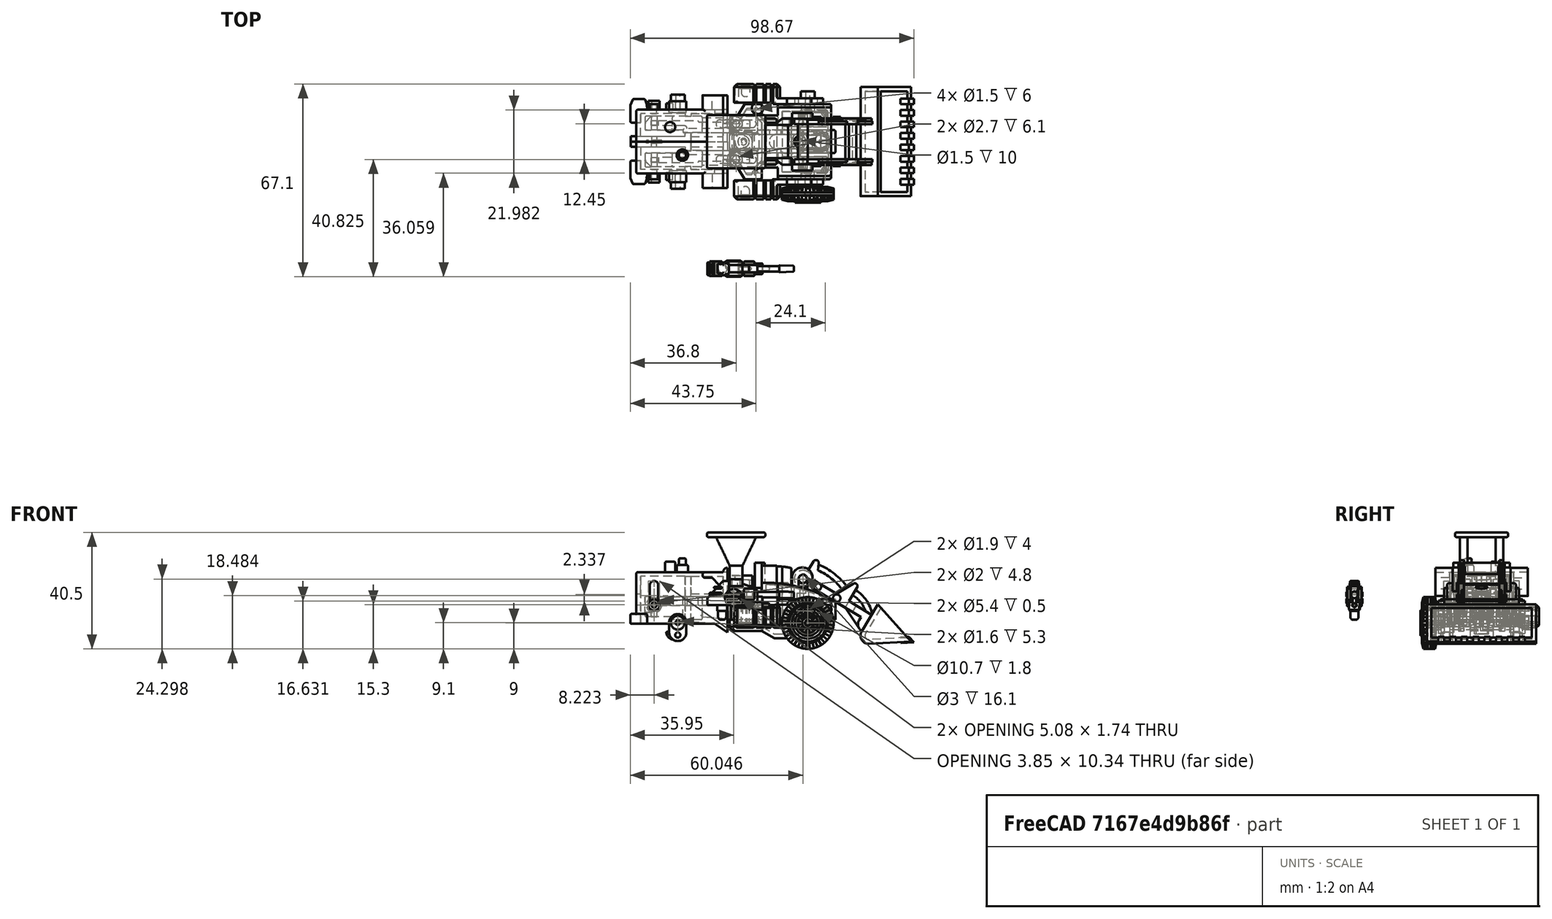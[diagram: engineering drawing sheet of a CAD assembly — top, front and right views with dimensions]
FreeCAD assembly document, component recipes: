
FREECAD ASSEMBLY — COMPONENT RECIPES ("Scrapper")

This assembly document has 14 components, labeled P0..P13 below (a component is one placed body or linked part). 14 of them carry a construction recipe — the FreeCAD feature program that regenerates the part from scratch, quoted from this document or its linked companion documents; the rest are supplied as boundary geometry only. No exploded tour is included for this assembly.
NOTE — document 4 of 4 of this assembly tour. The two overview renders and the header above are repeated from document 1; the component sections below continue where the previous document stopped.
COMPONENT P13 — recipe-attached ("Head", modeled in this document).
Construction recipe (the document's own serialized feature program — sketch geometry with constraints, then the solid features built on it; lengths are millimeters unless a unit is written):

FEATURE [Sketcher::SketchObject] Sketch256
  ArcFitTolerance = 1e-06
  AttachmentSupport = -> [XY_Plane009]
  FullyConstrained = true
  MakeInternals = false
  MapMode = 5
  sketch-geometry (6):
    g0: LineSegment StartX=0 StartY=0 StartZ=0 EndX=17 EndY=0 EndZ=0
    g1: LineSegment StartX=0 StartY=8 StartZ=0 EndX=17 EndY=8 EndZ=0
    g2: ArcOfCircle CenterX=17 CenterY=7.25 CenterZ=0 NormalX=0 NormalY=0 NormalZ=1 AngleXU=0 Radius=0.75 StartAngle=4.71239 EndAngle=7.85398
    g3: ArcOfCircle CenterX=17 CenterY=0.75 CenterZ=0 NormalX=0 NormalY=0 NormalZ=1 AngleXU=0 Radius=0.75 StartAngle=4.71239 EndAngle=7.85398
    g4: LineSegment StartX=0 StartY=8 StartZ=0 EndX=0 EndY=0 EndZ=0
    g5: LineSegment StartX=17 StartY=6.5 StartZ=0 EndX=17 EndY=1.5 EndZ=0
  constraints (19):
    c: Coincident(g0,g-1)
    c: PointOnObject(g0,g-1)
    c: PointOnObject(g1,g-2)
    c: Horizontal(g1)
    c: Coincident(g2,g1)
    c: Coincident(g3,g0)
    c: Coincident(g4,g1)
    c: Coincident(g4,g0)
    c: Coincident(g5,g2)
    c: Coincident(g5,g3)
    c: Vertical(g5)
    c: DistanceY(g4,g4) = 8
    c: DistanceY(g5,g5) = 5
    c: Diameter(g2) = 1.5
    c: Diameter(g3) = 1.5
    c: DistanceX(g3,g0) = 0
    c: DistanceX(g3,g3) = 0
    c: DistanceX(g0,g0) = 17
    c: DistanceX(g1,g1) = 17
FEATURE [PartDesign::Pad] Pad154
  Direction = (0,0,1)
  Length = 1
  Length2 = 10
  Profile = -> Sketch256
  ReferenceAxis = -> Sketch256 [N_Axis]
  Refine = true
  Suppressed = false
  Type = 0
FEATURE [Sketcher::SketchObject] Sketch257
  ArcFitTolerance = 1e-06
  AttachmentSupport = -> [Pad154]
  ExternalGeometry = -> [Pad154]
  FullyConstrained = true
  MakeInternals = false
  MapMode = 5
  Placement = pos=(0,0,1) rot=(0,0,1;0rad)
  sketch-geometry (4):
    g0: ArcOfCircle CenterX=3.2 CenterY=4 CenterZ=0 NormalX=0 NormalY=0 NormalZ=1 AngleXU=0 Radius=2.5 StartAngle=1.5708 EndAngle=4.71239
    g1: ArcOfCircle CenterX=11 CenterY=4 CenterZ=0 NormalX=0 NormalY=0 NormalZ=1 AngleXU=0 Radius=2.5 StartAngle=4.71239 EndAngle=7.85398
    g2: LineSegment StartX=3.2 StartY=6.5 StartZ=0 EndX=11 EndY=6.5 EndZ=0
    g3: LineSegment StartX=3.2 StartY=1.5 StartZ=0 EndX=11 EndY=1.5 EndZ=0
  constraints (11):
    c: Tangent(g0,g2) = 1.5708
    c: Tangent(g0,g3) = -1.5708
    c: Tangent(g1,g2) = 1.5708
    c: Tangent(g1,g3) = -1.5708
    c: Equal(g0,g1)
    c: Horizontal(g2)
    c: Diameter(g0) = 5
    c: DistanceX(g1,g-3) = 6
    c: DistanceX(g0,g1) = 7.8
    c: DistanceY(g-1,g-4) = 8
    c: DistanceY(g0,g-4) = 4
FEATURE [PartDesign::Pocket] Pocket106
  BaseFeature = -> Pad154
  Direction = (0,0,-1)
  Length = 5
  Length2 = 5
  Profile = -> Sketch257
  ReferenceAxis = -> Sketch257 [N_Axis]
  Refine = true
  Suppressed = false
  Type = 0
FEATURE [Sketcher::SketchObject] Sketch258
  ArcFitTolerance = 1e-06
  AttachmentSupport = -> [Pocket106]
  ExternalGeometry = -> [Pocket106]
  FullyConstrained = true
  MakeInternals = false
  MapMode = 5
  Placement = pos=(0,0,0) rot=(1,0,0;1.5708rad)
  sketch-geometry (4):
    g0: LineSegment StartX=0 StartY=1 StartZ=0 EndX=0 EndY=5 EndZ=0
    g1: LineSegment StartX=0 StartY=5 StartZ=0 EndX=9.5 EndY=5 EndZ=0
    g2: LineSegment StartX=9.5 StartY=5 StartZ=0 EndX=13.5 EndY=1 EndZ=0
    g3: LineSegment StartX=13.5 StartY=1 StartZ=0 EndX=0 EndY=1 EndZ=0
  constraints (11):
    c: Coincident(g0,g-3)
    c: PointOnObject(g0,g-2)
    c: Coincident(g1,g0)
    c: Horizontal(g1)
    c: Coincident(g2,g1)
    c: PointOnObject(g2,g-3)
    c: Coincident(g3,g2)
    c: Coincident(g3,g0)
    c: DistanceX(g2,g-3) = 3.5
    c: DistanceY(g0,g0) = 4
    c: Angle(g2,g3) = 0.785398
FEATURE [PartDesign::Pad] Pad155
  BaseFeature = -> Pocket106
  Direction = (0,-1,2e-16)
  Length = 8
  Length2 = 10
  Profile = -> Sketch258
  ReferenceAxis = -> Sketch258 [N_Axis]
  Refine = true
  Reversed = true
  Suppressed = false
  Type = 0
FEATURE [Sketcher::SketchObject] Sketch259
  ArcFitTolerance = 1e-06
  AttachmentSupport = -> [Pad155]
  ExternalGeometry = -> [Pad155]
  FullyConstrained = true
  MakeInternals = false
  MapMode = 5
  Placement = pos=(0,2e-16,1) rot=(1,0,0;3.14159rad)
  sketch-geometry (4):
    g0: ArcOfCircle CenterX=3.2 CenterY=-4 CenterZ=0 NormalX=0 NormalY=0 NormalZ=1 AngleXU=0 Radius=2.5 StartAngle=1.5708 EndAngle=4.71239
    g1: ArcOfCircle CenterX=11 CenterY=-4 CenterZ=0 NormalX=0 NormalY=0 NormalZ=1 AngleXU=0 Radius=2.5 StartAngle=4.71239 EndAngle=7.85398
    g2: LineSegment StartX=11 StartY=-1.5 StartZ=0 EndX=3.2 EndY=-1.5 EndZ=0
    g3: LineSegment StartX=11 StartY=-6.5 StartZ=0 EndX=3.2 EndY=-6.5 EndZ=0
  constraints (8):
    c: Tangent(g0,g-4) = -1.5708
    c: Coincident(g0,g-6)
    c: Coincident(g1,g-5)
    c: Tangent(g1,g-7) = -1.5708
    c: Coincident(g2,g0)
    c: Coincident(g3,g1)
    c: Coincident(g3,g-4)
    c: Coincident(g2,g1)
FEATURE [PartDesign::Pocket] Pocket107
  BaseFeature = -> Pad155
  Direction = (0,0,1)
  Length = 5
  Length2 = 5
  Profile = -> Sketch259
  ReferenceAxis = -> Sketch259 [N_Axis]
  Refine = true
  Suppressed = false
  Type = 0
FEATURE [Sketcher::SketchObject] Sketch260
  ArcFitTolerance = 1e-06
  AttachmentSupport = -> [Pocket107]
  ExternalGeometry = -> [Pocket107]
  FullyConstrained = true
  MakeInternals = false
  MapMode = 5
  Placement = pos=(17,0,0) rot=(0.57735,0.57735,0.57735;2.0944rad)
  sketch-geometry (4):
    g0: LineSegment StartX=1.5 StartY=5 StartZ=0 EndX=6.5 EndY=5 EndZ=0
    g1: LineSegment StartX=1.5 StartY=5 StartZ=0 EndX=1.5 EndY=1 EndZ=0
    g2: LineSegment StartX=6.5 StartY=5 StartZ=0 EndX=6.5 EndY=1 EndZ=0
    g3: LineSegment StartX=6.5 StartY=1 StartZ=0 EndX=1.5 EndY=1 EndZ=0
  constraints (8):
    c: Coincident(g0,g-3)
    c: Coincident(g0,g-4)
    c: Coincident(g1,g0)
    c: Coincident(g1,g-5)
    c: Coincident(g2,g0)
    c: Coincident(g2,g-5)
    c: Coincident(g3,g2)
    c: Coincident(g3,g1)
FEATURE [PartDesign::Pocket] Pocket108
  BaseFeature = -> Pocket107
  Direction = (-1,0,0)
  Length = 9
  Length2 = 5
  Profile = -> Sketch260
  ReferenceAxis = -> Sketch260 [N_Axis]
  Refine = true
  Suppressed = false
  Type = 0
FEATURE [Sketcher::SketchObject] Sketch261
  ArcFitTolerance = 1e-06
  AttachmentSupport = -> [Pocket108]
  ExternalGeometry = -> [Pocket108]
  FullyConstrained = true
  MakeInternals = false
  MapMode = 5
  Placement = pos=(0,1.1e-15,5) rot=(0,0,1;0rad)
  sketch-geometry (4):
    g0: LineSegment StartX=0 StartY=8 StartZ=0 EndX=-8 EndY=8 EndZ=0
    g1: LineSegment StartX=-8 StartY=8 StartZ=0 EndX=-8 EndY=0 EndZ=0
    g2: LineSegment StartX=-8 StartY=0 StartZ=0 EndX=0 EndY=0 EndZ=0
    g3: LineSegment StartX=0 StartY=0 StartZ=0 EndX=0 EndY=8 EndZ=0
  constraints (11):
    c: Coincident(g0,g1)
    c: Coincident(g1,g2)
    c: Coincident(g2,g3)
    c: Coincident(g3,g0)
    c: Horizontal(g0)
    c: Horizontal(g2)
    c: Vertical(g1)
    c: Vertical(g3)
    c: Coincident(g0,g-3)
    c: PointOnObject(g1,g-1)
    c: DistanceX(g0,g0) = 8
FEATURE [PartDesign::Pad] Pad156
  BaseFeature = -> Pocket108
  Direction = (0,0,1)
  Length = 1.5
  Length2 = 10
  Profile = -> Sketch261
  ReferenceAxis = -> Sketch261 [N_Axis]
  Refine = true
  Reversed = true
  Suppressed = false
  Type = 0
FEATURE [Sketcher::SketchObject] Sketch262
  ArcFitTolerance = 1e-06
  AttachmentSupport = -> [Pad156]
  ExternalGeometry = -> [Pad156]
  FullyConstrained = true
  MakeInternals = false
  MapMode = 5
  Placement = pos=(-8,0,0) rot=(0.57735,-0.57735,-0.57735;2.0944rad)
  sketch-geometry (4):
    g0: LineSegment StartX=-8 StartY=7 StartZ=0 EndX=-8 EndY=0 EndZ=0
    g1: LineSegment StartX=-8 StartY=0 StartZ=0 EndX=-1.8e-15 EndY=0 EndZ=0
    g2: LineSegment StartX=-1.8e-15 StartY=0 StartZ=0 EndX=-1.8e-15 EndY=7 EndZ=0
    g3: LineSegment StartX=-1.8e-15 StartY=7 StartZ=0 EndX=-8 EndY=7 EndZ=0
  constraints (12):
    c: Coincident(g0,g1)
    c: Coincident(g1,g2)
    c: Coincident(g2,g3)
    c: Coincident(g3,g0)
    c: Vertical(g0)
    c: Vertical(g2)
    c: Horizontal(g1)
    c: Horizontal(g3)
    c: DistanceX(g3,g3) = 8
    c: DistanceY(g0,g0) = 7
    c: PointOnObject(g-4,g0)
    c: DistanceY(g-4,g0) = 2
FEATURE [PartDesign::Pad] Pad157
  BaseFeature = -> Pad156
  Direction = (-1,0,0)
  Length = 1.5
  Length2 = 10
  Profile = -> Sketch262
  ReferenceAxis = -> Sketch262 [N_Axis]
  Refine = true
  Suppressed = false
  Type = 0
FEATURE [PartDesign::Fillet] Fillet009
  Base = -> Pad157 [Edge56,Edge57,Edge5,Edge50,Edge7,Edge51]
  BaseFeature = -> Pad157
  Radius = 0.5
  Refine = true
  SupportTransform = false
  Suppressed = false
  UseAllEdges = false
FEATURE [Sketcher::SketchObject] Sketch263
  ArcFitTolerance = 1e-06
  AttachmentSupport = -> [Fillet009]
  ExternalGeometry = -> [Fillet009]
  FullyConstrained = true
  MakeInternals = false
  MapMode = 5
  Placement = pos=(0,0,5) rot=(0,0,1;0rad)
  sketch-geometry (1):
    g0: Circle CenterX=-4.55 CenterY=4 CenterZ=0 NormalX=0 NormalY=0 NormalZ=1 AngleXU=0 Radius=2.35
  constraints (5):
    c: Diameter(g0) = 4.7
    c: DistanceY(g-5,g-5) = 7
    c: DistanceY(g0,g-5) = 3.5
    c: Radius(g-6) = 2.5
    c: DistanceX(g0,g-6) = 7.75
FEATURE [PartDesign::Pocket] Pocket109
  BaseFeature = -> Fillet009
  Direction = (0,0,-1)
  Length = 0.7
  Length2 = 5
  Profile = -> Sketch263
  ReferenceAxis = -> Sketch263 [N_Axis]
  Refine = true
  Suppressed = false
  Type = 0
FEATURE [Sketcher::SketchObject] Sketch265
  ArcFitTolerance = 1e-06
  AttachmentSupport = -> [Pocket109]
  ExternalGeometry = -> [Pocket109]
  FullyConstrained = true
  MakeInternals = false
  MapMode = 5
  Placement = pos=(0,0,3.5) rot=(1,0,0;3.14159rad)
  sketch-geometry (6):
    g0: LineSegment StartX=0 StartY=-0.5 StartZ=0 EndX=0 EndY=-7.5 EndZ=0
    g1: LineSegment StartX=0 StartY=-7.5 StartZ=0 EndX=-4 EndY=-7.5 EndZ=0
    g2: LineSegment StartX=-4 StartY=-7.5 StartZ=0 EndX=-7.25 EndY=-6 EndZ=0
    g3: LineSegment StartX=-7.25 StartY=-6 StartZ=0 EndX=-7.25 EndY=-2 EndZ=0
    g4: LineSegment StartX=-7.25 StartY=-2 StartZ=0 EndX=-4 EndY=-0.5 EndZ=0
    g5: LineSegment StartX=-4 StartY=-0.5 StartZ=0 EndX=0 EndY=-0.5 EndZ=0
  constraints (19):
    c: PointOnObject(g0,g-3)
    c: PointOnObject(g0,g-3)
    c: Coincident(g1,g0)
    c: Horizontal(g1)
    c: Coincident(g2,g1)
    c: Coincident(g3,g2)
    c: Vertical(g3)
    c: Coincident(g4,g3)
    c: Coincident(g5,g4)
    c: Coincident(g5,g0)
    c: Horizontal(g5)
    c: DistanceY(g-5,g0) = 0.5
    c: DistanceY(g0,g-1) = 0.5
    c: DistanceX(g5,g5) = 4
    c: DistanceX(g1,g1) = 4
    c: DistanceY(g-7,g-7) = 8
    c: DistanceY(g3,g-4) = 2
    c: DistanceY(g-5,g2) = 2
    c: DistanceX(g-6,g3) = 0.75
FEATURE [PartDesign::Pad] Pad158
  BaseFeature = -> Pocket109
  Direction = (0,0,-1)
  Length = 1
  Length2 = 10
  Profile = -> Sketch265
  ReferenceAxis = -> Sketch265 [N_Axis]
  Refine = true
  Suppressed = false
  Type = 0
FEATURE [Sketcher::SketchObject] Sketch266
  ArcFitTolerance = 1e-06
  AttachmentSupport = -> [Pad158]
  ExternalGeometry = -> [Pad158]
  FullyConstrained = true
  MakeInternals = false
  MapMode = 5
  Placement = pos=(0,0.5,0) rot=(1,0,0;1.5708rad)
  sketch-geometry (4):
    g0: LineSegment StartX=0 StartY=2.5 StartZ=0 EndX=-4 EndY=2.5 EndZ=0
    g1: LineSegment StartX=-3 StartY=1.5 StartZ=0 EndX=0 EndY=1.5 EndZ=0
    g2: LineSegment StartX=0 StartY=1.5 StartZ=0 EndX=0 EndY=2.5 EndZ=0
    g3: LineSegment StartX=-4 StartY=2.5 StartZ=0 EndX=-3 EndY=1.5 EndZ=0
  constraints (11):
    c: DistanceY(g-3,g-3) = 3.5
    c: Coincident(g1,g2)
    c: Coincident(g2,g0)
    c: Horizontal(g1)
    c: Vertical(g2)
    c: Coincident(g0,g-4)
    c: Coincident(g0,g-4)
    c: DistanceY(g1,g0) = 1
    c: Coincident(g3,g0)
    c: Coincident(g3,g1)
    c: Angle(g3,g0) = 0.785398
FEATURE [PartDesign::Pad] Pad159
  BaseFeature = -> Pad158
  Direction = (0,-1,2e-16)
  Length = 1.3
  Length2 = 10
  Profile = -> Sketch266
  ReferenceAxis = -> Sketch266 [N_Axis]
  Refine = true
  Reversed = true
  Suppressed = false
  Type = 0
FEATURE [Sketcher::SketchObject] Sketch267
  ArcFitTolerance = 1e-06
  AttachmentSupport = -> [Pad159]
  ExternalGeometry = -> [Pad159]
  FullyConstrained = true
  MakeInternals = false
  MapMode = 5
  Placement = pos=(0,7.5,0) rot=(0,0.707107,0.707107;3.14159rad)
  sketch-geometry (4):
    g0: LineSegment StartX=4 StartY=2.5 StartZ=0 EndX=3 EndY=1.5 EndZ=0
    g1: LineSegment StartX=3 StartY=1.5 StartZ=0 EndX=0 EndY=1.5 EndZ=0
    g2: LineSegment StartX=0 StartY=1.5 StartZ=0 EndX=0 EndY=2.5 EndZ=0
    g3: LineSegment StartX=0 StartY=2.5 StartZ=0 EndX=4 EndY=2.5 EndZ=0
  constraints (8):
    c: Coincident(g0,g-6)
    c: Coincident(g0,g-5)
    c: Coincident(g1,g0)
    c: Coincident(g1,g-4)
    c: Coincident(g2,g1)
    c: Coincident(g2,g-6)
    c: Coincident(g3,g2)
    c: Coincident(g3,g0)
FEATURE [PartDesign::Pad] Pad160
  BaseFeature = -> Pad159
  Direction = (0,1,-2e-16)
  Length = 1.3
  Length2 = 10
  Profile = -> Sketch267
  ReferenceAxis = -> Sketch267 [N_Axis]
  Refine = true
  Reversed = true
  Suppressed = false
  Type = 0
FEATURE [Sketcher::SketchObject] Sketch268
  ArcFitTolerance = 1e-06
  AttachmentSupport = -> [Pad160]
  ExternalGeometry = -> [Pad160]
  FullyConstrained = true
  MakeInternals = false
  MapMode = 5
  Placement = pos=(0,3e-16,1.5) rot=(1,0,0;3.14159rad)
  sketch-geometry (8):
    g0: LineSegment StartX=0 StartY=-0.5 StartZ=0 EndX=0 EndY=-1.8 EndZ=0
    g1: LineSegment StartX=0 StartY=-1.8 StartZ=0 EndX=-2.35 EndY=-1.8 EndZ=0
    g2: LineSegment StartX=0 StartY=-0.5 StartZ=0 EndX=-2.35 EndY=-0.5 EndZ=0
    g3: ArcOfCircle CenterX=-2.35 CenterY=-1.15 CenterZ=0 NormalX=0 NormalY=0 NormalZ=1 AngleXU=0 Radius=0.65 StartAngle=1.5708 EndAngle=4.71239
    g4: LineSegment StartX=0 StartY=-6.2 StartZ=0 EndX=0 EndY=-7.5 EndZ=0
    g5: LineSegment StartX=0 StartY=-7.5 StartZ=0 EndX=-2.35 EndY=-7.5 EndZ=0
    g6: LineSegment StartX=0 StartY=-6.2 StartZ=0 EndX=-2.35 EndY=-6.2 EndZ=0
    g7: ArcOfCircle CenterX=-2.35 CenterY=-6.85 CenterZ=0 NormalX=0 NormalY=0 NormalZ=1 AngleXU=0 Radius=0.65 StartAngle=1.5708 EndAngle=4.71239
  constraints (23):
    c: PointOnObject(g0,g-4)
    c: Coincident(g0,g-6)
    c: Vertical(g0)
    c: PointOnObject(g1,g-6)
    c: Coincident(g2,g0)
    c: PointOnObject(g2,g-4)
    c: Coincident(g3,g1)
    c: Coincident(g2,g3)
    c: Tangent(g3,g-5)
    c: DistanceX(g3,g2) = 0
    c: DistanceX(g3,g1) = 0
    c: Coincident(g1,g0)
    c: Coincident(g4,g-8)
    c: Coincident(g4,g-9)
    c: Coincident(g5,g4)
    c: PointOnObject(g5,g-9)
    c: PointOnObject(g6,g-7)
    c: Coincident(g7,g6)
    c: Coincident(g7,g5)
    c: DistanceX(g7,g7) = 0
    c: DistanceX(g7,g5) = 0
    c: Tangent(g7,g-10)
    c: Coincident(g6,g4)
FEATURE [PartDesign::Pad] Pad161
  BaseFeature = -> Pad160
  Direction = (0,0,-1)
  Length = 1
  Length2 = 10
  Profile = -> Sketch268
  ReferenceAxis = -> Sketch268 [N_Axis]
  Refine = true
  Suppressed = false
  Type = 0
FEATURE [Sketcher::SketchObject] Sketch269
  ArcFitTolerance = 1e-06
  AttachmentSupport = -> [Pad161]
  ExternalGeometry = -> [Pad161]
  FullyConstrained = true
  MakeInternals = false
  MapMode = 5
  Placement = pos=(0,0,2.5) rot=(1,0,0;3.14159rad)
  sketch-geometry (6):
    g0: LineSegment StartX=-4 StartY=-0.5 StartZ=0 EndX=-6.95 EndY=-1.86154 EndZ=0
    g1: LineSegment StartX=-6.95 StartY=-1.86154 StartZ=0 EndX=-6.95 EndY=-1.11154 EndZ=0
    g2: LineSegment StartX=-4 StartY=-0.5 StartZ=0 EndX=-6.95 EndY=-1.11154 EndZ=0
    g3: LineSegment StartX=-4 StartY=-7.5 StartZ=0 EndX=-6.95 EndY=-6.13846 EndZ=0
    g4: LineSegment StartX=-6.95 StartY=-6.13846 StartZ=0 EndX=-6.95 EndY=-6.88846 EndZ=0
    g5: LineSegment StartX=-4 StartY=-7.5 StartZ=0 EndX=-6.95 EndY=-6.88846 EndZ=0
  constraints (16):
    c: Coincident(g0,g-3)
    c: PointOnObject(g0,g-3)
    c: Coincident(g1,g0)
    c: Vertical(g1)
    c: Coincident(g2,g0)
    c: Coincident(g2,g1)
    c: DistanceY(g1,g1) = 0.75
    c: DistanceX(g-3,g0) = 0.3
    c: Coincident(g3,g-4)
    c: PointOnObject(g3,g-4)
    c: Coincident(g4,g3)
    c: Vertical(g4)
    c: Coincident(g5,g3)
    c: Coincident(g5,g4)
    c: DistanceX(g-4,g3) = 0.3
    c: DistanceY(g4,g3) = 0.75
FEATURE [PartDesign::Pad] Pad162
  BaseFeature = -> Pad161
  Direction = (0,0,-1)
  Length = 1
  Length2 = 10
  Profile = -> Sketch269
  ReferenceAxis = -> Sketch269 [N_Axis]
  Refine = true
  Reversed = true
  Suppressed = false
  Type = 0
FEATURE [Sketcher::SketchObject] Sketch270
  ArcFitTolerance = 1e-06
  AttachmentOffset = pos=(0,0,1) rot=(0,0,1;0rad)
  AttachmentSupport = -> [Pad162]
  ExternalGeometry = -> [Pad162]
  FullyConstrained = true
  MakeInternals = false
  MapMode = 5
  Placement = pos=(-3.97516,8.61284,0) rot=(-0.153467,0.69873,0.69873;3.44615rad)
  sketch-geometry (3):
    g0: LineSegment StartX=0.488901 StartY=2.5 StartZ=0 EndX=4.06836 EndY=3.3 EndZ=0
    g1: LineSegment StartX=0.488901 StartY=2.5 StartZ=0 EndX=4.06836 EndY=2.5 EndZ=0
    g2: LineSegment StartX=4.06836 StartY=2.5 StartZ=0 EndX=4.06836 EndY=3.3 EndZ=0
  constraints (7):
    c: Coincident(g0,g-3)
    c: Coincident(g1,g0)
    c: Coincident(g1,g-6)
    c: PointOnObject(g0,g-6)
    c: Coincident(g2,g1)
    c: Coincident(g2,g0)
    c: DistanceY(g2,g2) = 0.8
FEATURE [PartDesign::Pocket] Pocket111
  BaseFeature = -> Pad162
  Direction = (0.419058,-0.907959,0)
  Length = 1
  Length2 = 5
  Profile = -> Sketch270
  ReferenceAxis = -> Sketch270 [N_Axis]
  Refine = true
  Suppressed = false
  Type = 0
FEATURE [Sketcher::SketchObject] Sketch271
  ArcFitTolerance = 1e-06
  AttachmentOffset = pos=(0,0,1) rot=(0,0,1;0rad)
  AttachmentSupport = -> [Pocket111]
  ExternalGeometry = -> [Pocket111]
  FullyConstrained = true
  MakeInternals = false
  MapMode = 5
  Placement = pos=(-0.931253,-2.01772,-3e-16) rot=(0.954992,-0.209751,-0.209751;1.61683rad)
  sketch-geometry (3):
    g0: LineSegment StartX=-3.84137 StartY=2.5 StartZ=0 EndX=-7.42082 EndY=2.5 EndZ=0
    g1: LineSegment StartX=-3.84137 StartY=2.5 StartZ=0 EndX=-7.42082 EndY=3.3 EndZ=0
    g2: LineSegment StartX=-7.42082 StartY=2.5 StartZ=0 EndX=-7.42082 EndY=3.3 EndZ=0
  constraints (7):
    c: Coincident(g0,g-4)
    c: Coincident(g0,g-3)
    c: Coincident(g1,g-4)
    c: PointOnObject(g1,g-3)
    c: Coincident(g2,g-3)
    c: Coincident(g2,g1)
    c: DistanceY(g2,g2) = 0.8
FEATURE [PartDesign::Pocket] Pocket112
  BaseFeature = -> Pocket111
  Direction = (0.419058,0.907959,3e-16)
  Length = 1
  Length2 = 5
  Profile = -> Sketch271
  ReferenceAxis = -> Sketch271 [N_Axis]
  Refine = true
  Suppressed = false
  Type = 0
FEATURE [Sketcher::SketchObject] Sketch272
  ArcFitTolerance = 1e-06
  AttachmentSupport = -> [Pocket112]
  ExternalGeometry = -> [Pocket112]
  FullyConstrained = true
  MakeInternals = false
  MapMode = 5
  Placement = pos=(-0.0654326,-0.31564,0) rot=(0.989644,-0.101498,-0.101498;1.58121rad)
  sketch-geometry (4):
    g0: LineSegment StartX=-4.51822 StartY=3.5 StartZ=0 EndX=-6.51822 EndY=3.5 EndZ=0
    g1: LineSegment StartX=-6.51822 StartY=3.5 StartZ=0 EndX=-6.51822 EndY=3.1 EndZ=0
    g2: LineSegment StartX=-6.51822 StartY=3.1 StartZ=0 EndX=-4.51822 EndY=3.1 EndZ=0
    g3: LineSegment StartX=-4.51822 StartY=3.1 StartZ=0 EndX=-4.51822 EndY=3.5 EndZ=0
  constraints (12):
    c: Coincident(g0,g1)
    c: Coincident(g1,g2)
    c: Coincident(g2,g3)
    c: Coincident(g3,g0)
    c: Horizontal(g0)
    c: Horizontal(g2)
    c: Vertical(g1)
    c: Vertical(g3)
    c: PointOnObject(g0,g-3)
    c: DistanceX(g2,g2) = 2
    c: DistanceY(g3,g3) = 0.4
    c: DistanceX(g0,g-5) = 0.5
FEATURE [PartDesign::Pad] Pad163
  BaseFeature = -> Pocket112
  Direction = (-0.202986,-0.979182,2e-16)
  Length = 0.2
  Length2 = 10
  Profile = -> Sketch272
  ReferenceAxis = -> Sketch272 [N_Axis]
  Refine = true
  Suppressed = false
  Type = 0
FEATURE [Sketcher::SketchObject] Sketch273
  ArcFitTolerance = 1e-06
  AttachmentSupport = -> [Pad163]
  ExternalGeometry = -> [Pad163]
  FullyConstrained = true
  MakeInternals = false
  MapMode = 5
  Placement = pos=(-1.65551,7.98602,0) rot=(-0.072331,0.705255,0.705255;3.286rad)
  sketch-geometry (4):
    g0: LineSegment StartX=4.89434 StartY=3.5 StartZ=0 EndX=2.89434 EndY=3.5 EndZ=0
    g1: LineSegment StartX=2.89434 StartY=3.5 StartZ=0 EndX=2.89434 EndY=3.1 EndZ=0
    g2: LineSegment StartX=2.89434 StartY=3.1 StartZ=0 EndX=4.89434 EndY=3.1 EndZ=0
    g3: LineSegment StartX=4.89434 StartY=3.1 StartZ=0 EndX=4.89434 EndY=3.5 EndZ=0
  constraints (12):
    c: Coincident(g0,g1)
    c: Coincident(g1,g2)
    c: Coincident(g2,g3)
    c: Coincident(g3,g0)
    c: Horizontal(g0)
    c: Horizontal(g2)
    c: Vertical(g1)
    c: Vertical(g3)
    c: PointOnObject(g0,g-4)
    c: DistanceX(g2,g2) = 2
    c: DistanceY(g1,g1) = 0.4
    c: DistanceX(g-4,g0) = 0.5
FEATURE [PartDesign::Pad] Pad164
  BaseFeature = -> Pad163
  Direction = (-0.202986,0.979182,-2e-16)
  Length = 0.2
  Length2 = 10
  Profile = -> Sketch273
  ReferenceAxis = -> Sketch273 [N_Axis]
  Refine = true
  Suppressed = false
  Type = 0
FEATURE [Sketcher::SketchObject] Sketch274
  ArcFitTolerance = 1e-06
  AttachmentSupport = -> [Pad164]
  ExternalGeometry = -> [Pad164]
  FullyConstrained = true
  MakeInternals = false
  MapMode = 5
  Placement = pos=(0,0,2.5) rot=(1,0,0;3.14159rad)
  sketch-geometry (4):
    g0: LineSegment StartX=-4.5 StartY=-1.25 StartZ=0 EndX=-4.5 EndY=-6.75 EndZ=0
    g1: LineSegment StartX=-4.5 StartY=-6.75 StartZ=0 EndX=-6.75 EndY=-5.71154 EndZ=0
    g2: LineSegment StartX=-6.75 StartY=-5.71154 StartZ=0 EndX=-6.75 EndY=-2.28846 EndZ=0
    g3: LineSegment StartX=-6.75 StartY=-2.28846 StartZ=0 EndX=-4.5 EndY=-1.25 EndZ=0
  constraints (13):
    c: Vertical(g0)
    c: Coincident(g1,g0)
    c: Coincident(g2,g1)
    c: Vertical(g2)
    c: Coincident(g3,g2)
    c: Coincident(g3,g0)
    c: Parallel(g-3,g3)
    c: Parallel(g-5,g1)
    c: DistanceX(g-4,g2) = 0.5
    c: DistanceX(g0,g-6) = 0.5
    c: DistanceY(g-7,g-6) = 7
    c: DistanceY(g0,g0) = 5.5
    c: DistanceY(g0,g-6) = 0.75
FEATURE [PartDesign::Pad] Pad165
  BaseFeature = -> Pad164
  Direction = (0,0,-1)
  Length = 2
  Length2 = 10
  Profile = -> Sketch274
  ReferenceAxis = -> Sketch274 [N_Axis]
  Refine = true
  Suppressed = false
  Type = 0
FEATURE [PartDesign::Draft] Draft
  Angle = 15
  Base = -> Pad165 [Face62,Face60]
  BaseFeature = -> Pad165
  NeutralPlane = -> Pad165 [Face34]
  Refine = true
  SupportTransform = false
  Suppressed = false
FEATURE [Sketcher::SketchObject] Sketch275
  ArcFitTolerance = 1e-06
  AttachmentSupport = -> [Draft]
  ExternalGeometry = -> [Draft]
  FullyConstrained = true
  MakeInternals = false
  MapMode = 5
  Placement = pos=(0,8e-16,0) rot=(1,0,0;1.5708rad)
  sketch-geometry (3):
    g0: LineSegment StartX=-6.75 StartY=2.5 StartZ=0 EndX=-6.75 EndY=0.5 EndZ=0
    g1: LineSegment StartX=-6.75 StartY=0.5 StartZ=0 EndX=-6.2141 EndY=0.5 EndZ=0
    g2: LineSegment StartX=-6.2141 StartY=0.5 StartZ=0 EndX=-6.75 EndY=2.5 EndZ=0
  constraints (7):
    c: Coincident(g0,g-3)
    c: Coincident(g0,g-4)
    c: Coincident(g1,g0)
    c: PointOnObject(g1,g-4)
    c: Coincident(g2,g1)
    c: Coincident(g2,g0)
    c: Angle(g0,g2) = 0.261799
FEATURE [PartDesign::Pocket] Pocket113
  BaseFeature = -> Draft
  Direction = (0,1,-2e-16)
  Length = 7
  Length2 = 5
  Profile = -> Sketch275
  ReferenceAxis = -> Sketch275 [N_Axis]
  Refine = true
  Suppressed = false
  Type = 0
FEATURE [Sketcher::SketchObject] Sketch276
  ArcFitTolerance = 1e-06
  AttachmentSupport = -> [Pocket113]
  ExternalGeometry = -> [Pocket113]
  FullyConstrained = true
  MakeInternals = false
  MapMode = 5
  Placement = pos=(0,0,2.5) rot=(1,0,0;3.14159rad)
  sketch-geometry (4):
    g0: LineSegment StartX=-6.2141 StartY=-3 StartZ=0 EndX=-7.7141 EndY=-3 EndZ=0
    g1: LineSegment StartX=-7.7141 StartY=-3 StartZ=0 EndX=-7.7141 EndY=-5 EndZ=0
    g2: LineSegment StartX=-7.7141 StartY=-5 StartZ=0 EndX=-6.2141 EndY=-5 EndZ=0
    g3: LineSegment StartX=-6.2141 StartY=-5 StartZ=0 EndX=-6.2141 EndY=-3 EndZ=0
  constraints (13):
    c: Coincident(g0,g1)
    c: Coincident(g1,g2)
    c: Coincident(g2,g3)
    c: Coincident(g3,g0)
    c: Horizontal(g0)
    c: Horizontal(g2)
    c: Vertical(g1)
    c: Vertical(g3)
    c: PointOnObject(g0,g-5)
    c: DistanceY(g1,g1) = 2
    c: DistanceX(g0,g0) = 1.5
    c: DistanceY(g-3,g-3) = 4
    c: DistanceY(g0,g-3) = 1
FEATURE [PartDesign::Pad] Pad166
  BaseFeature = -> Pocket113
  Direction = (0,0,-1)
  Length = 1
  Length2 = 10
  Profile = -> Sketch276
  ReferenceAxis = -> Sketch276 [N_Axis]
  Refine = true
  Reversed = true
  Suppressed = false
  Type = 0
FEATURE [PartDesign::Pad] Pad167
  BaseFeature = -> Pad166
  Direction = (0,0,-1)
  Length = 1
  Length2 = 10
  Profile = -> Sketch276
  ReferenceAxis = -> Sketch276 [N_Axis]
  Refine = true
  Suppressed = false
  Type = 0
FEATURE [Sketcher::SketchObject] Sketch277
  ArcFitTolerance = 1e-06
  AttachmentSupport = -> [Pad167]
  ExternalGeometry = -> [Pad167]
  FullyConstrained = true
  MakeInternals = false
  MapMode = 5
  Placement = pos=(0,0,1.5) rot=(1,0,0;3.14159rad)
  sketch-geometry (14):
    g0: ArcOfCircle CenterX=-6.48205 CenterY=-4 CenterZ=0 NormalX=0 NormalY=0 NormalZ=1 AngleXU=0 Radius=0.3 StartAngle=1.5708 EndAngle=4.71239
    g1: LineSegment StartX=-6.48205 StartY=-3.4 StartZ=0 EndX=-6.88205 EndY=-3.4 EndZ=0
    g2: LineSegment StartX=-6.48205 StartY=-4.6 StartZ=0 EndX=-6.88205 EndY=-4.6 EndZ=0
    g3: ArcOfCircle CenterX=-6.88205 CenterY=-4.3 CenterZ=0 NormalX=0 NormalY=0 NormalZ=1 AngleXU=0 Radius=0.3 StartAngle=3.14159 EndAngle=4.71239
    g4: ArcOfCircle CenterX=-6.88205 CenterY=-3.7 CenterZ=0 NormalX=0 NormalY=0 NormalZ=1 AngleXU=0 Radius=0.3 StartAngle=1.5708 EndAngle=3.14159
    g5: LineSegment StartX=-7.18205 StartY=-3.7 StartZ=0 EndX=-7.18205 EndY=-4.3 EndZ=0
    g6: LineSegment StartX=-6.48205 StartY=-3.7 StartZ=0 EndX=-6.48205 EndY=-4.3 EndZ=0
    g7: LineSegment StartX=-6.48205 StartY=-4.6 StartZ=0 EndX=-6.48205 EndY=-5 EndZ=0
    g8: LineSegment StartX=-6.48205 StartY=-3 StartZ=0 EndX=-6.48205 EndY=-3.4 EndZ=0
    g9: LineSegment StartX=-6.48205 StartY=-3 StartZ=0 EndX=-7.28205 EndY=-3 EndZ=0
    g10: LineSegment StartX=-6.48205 StartY=-5 StartZ=0 EndX=-7.28205 EndY=-5 EndZ=0
    g11: ArcOfCircle CenterX=-7.28205 CenterY=-4.7 CenterZ=0 NormalX=0 NormalY=0 NormalZ=1 AngleXU=0 Radius=0.3 StartAngle=3.14159 EndAngle=4.71239
    g12: ArcOfCircle CenterX=-7.28205 CenterY=-3.3 CenterZ=0 NormalX=0 NormalY=0 NormalZ=1 AngleXU=0 Radius=0.3 StartAngle=1.5708 EndAngle=3.14159
    g13: LineSegment StartX=-7.58205 StartY=-3.3 StartZ=0 EndX=-7.58205 EndY=-4.7 EndZ=0
  constraints (46):
    c: PointOnObject(g0,g-3)
    c: PointOnObject(g0,g-3)
    c: PointOnObject(g1,g-3)
    c: Horizontal(g1)
    c: PointOnObject(g2,g-3)
    c: Horizontal(g2)
    c: Coincident(g3,g2)
    c: Coincident(g4,g1)
    c: Coincident(g5,g4)
    c: Coincident(g5,g3)
    c: Vertical(g5)
    c: DistanceX(g2,g3) = 0
    c: Radius(g0) = 0.3
    c: PointOnObject(g0,g-3)
    c: DistanceY(g3,g3) = 0
    c: Radius(g3) = 0.3
    c: Radius(g4) = 0.3
    c: DistanceX(g4,g1) = 0
    c: DistanceY(g4,g4) = 0
    c: DistanceY(g-5,g-5) = 2
    c: DistanceY(g0,g-4) = 1
    c: DistanceY(g5,g5) = 0.6
    c: DistanceY(g0,g1) = 0.3
    c: DistanceX(g1,g1) = 0.4
    c: Coincident(g6,g0)
    c: Coincident(g6,g0)
    c: Coincident(g7,g2)
    c: Coincident(g7,g-6)
    c: Coincident(g8,g1)
    c: Coincident(g9,g8)
    c: PointOnObject(g9,g-4)
    c: Coincident(g10,g7)
    c: PointOnObject(g10,g-6)
    c: Coincident(g11,g10)
    c: Coincident(g12,g9)
    c: Coincident(g13,g12)
    c: Coincident(g13,g11)
    c: Vertical(g13)
    c: DistanceX(g12,g9) = 0
    c: DistanceX(g11,g10) = 0
    c: Radius(g11) = 0.3
    c: Radius(g12) = 0.3
    c: DistanceY(g12,g12) = 0
    c: DistanceY(g11,g11) = 0
    c: DistanceX(g9,g9) = 0.8
    c: Coincident(g8,g-4)
FEATURE [PartDesign::SubShapeBinder] Binder004
  BindCopyOnChange = 0
  BindMode = 2
  ClaimChildren = false
  Context = -> Part [Body016.Binder004.]
  Fuse = false
  MakeFace = true
  OffsetFill = false
  OffsetIntersection = false
  OffsetJoinType = 0
  OffsetOpenResult = false
  PartialLoad = false
  Refine = true
  Relative = true
  _Version = 2
FEATURE [Sketcher::SketchObject] Sketch343
  ArcFitTolerance = 1e-06
  AttachmentSupport = -> [Binder004]
  ExternalGeometry = -> [Binder004]
  FullyConstrained = true
  MakeInternals = false
  MapMode = 5
  Placement = pos=(0,0,-2.5) rot=(1,0,0;3.14159rad)
  sketch-geometry (7):
    g0: LineSegment StartX=-8 StartY=2.2 StartZ=0 EndX=-8 EndY=-2.2 EndZ=0
    g1: LineSegment StartX=-4.75 StartY=-2.2 StartZ=0 EndX=-5.75 EndY=-0.901388 EndZ=0
    g2: LineSegment StartX=-4.75 StartY=2.2 StartZ=0 EndX=-5.75 EndY=0.901388 EndZ=0
    g3: ArcOfCircle CenterX=-4.25 CenterY=0 CenterZ=0 NormalX=0 NormalY=0 NormalZ=1 AngleXU=0 Radius=1.75 StartAngle=2.60049 EndAngle=3.68269
    g4: LineSegment [constr] StartX=-8 StartY=1.4e-15 StartZ=0 EndX=-6 EndY=1.4e-15 EndZ=0
    g5: LineSegment StartX=-4.75 StartY=-2.2 StartZ=0 EndX=-8 EndY=-2.2 EndZ=0
    g6: LineSegment StartX=-4.75 StartY=2.2 StartZ=0 EndX=-8 EndY=2.2 EndZ=0
  constraints (20):
    c: Coincident(g0,g-5)
    c: Coincident(g3,g2)
    c: Coincident(g3,g1)
    c: PointOnObject(g3,g-1)
    c: Symmetric(g0,g0,g4)
    c: PointOnObject(g4,g3)
    c: Horizontal(g4)
    c: DistanceX(g2,g1) = 0
    c: Radius(g3) = 1.75
    c: PointOnObject(g2,g-3)
    c: PointOnObject(g1,g-5)
    c: Coincident(g5,g1)
    c: Coincident(g5,g0)
    c: Coincident(g6,g2)
    c: Coincident(g6,g0)
    c: Coincident(g0,g-4)
    c: DistanceX(g2,g-3) = 0.75
    c: DistanceX(g1,g-5) = 0.75
    c: DistanceX(g4,g2) = 0.25
    c: DistanceX(g2,g2) = 1
FEATURE [PartDesign::Pad] Pad229
  Direction = (0,0,-1)
  Length = 2
  Length2 = 10
  Profile = -> Sketch343
  ReferenceAxis = -> Sketch343 [N_Axis]
  Refine = true
  Suppressed = false
  Type = 0
FEATURE [Sketcher::SketchObject] Sketch344
  ArcFitTolerance = 1e-06
  AttachmentSupport = -> [Pad229]
  ExternalGeometry = -> [Pad229]
  FullyConstrained = true
  MakeInternals = false
  MapMode = 5
  Placement = pos=(-8,0,0) rot=(0.57735,-0.57735,-0.57735;2.0944rad)
  sketch-geometry (5):
    g0: ArcOfCircle CenterX=0.828312 CenterY=-0.586702 CenterZ=0 NormalX=0 NormalY=0 NormalZ=1 AngleXU=0 Radius=4 StartAngle=3.85356 EndAngle=4.5038
    g1: ArcOfCircle CenterX=-0.828312 CenterY=-0.586702 CenterZ=0 NormalX=0 NormalY=0 NormalZ=1 AngleXU=0 Radius=4 StartAngle=4.92098 EndAngle=5.57122
    g2: LineSegment StartX=2.2 StartY=-3.2 StartZ=0 EndX=2.2 EndY=-4.5 EndZ=0
    g3: LineSegment StartX=2.2 StartY=-4.5 StartZ=0 EndX=-2.2 EndY=-4.5 EndZ=0
    g4: LineSegment StartX=-2.2 StartY=-4.5 StartZ=0 EndX=-2.2 EndY=-3.2 EndZ=0
  constraints (14):
    c: PointOnObject(g0,g-3)
    c: Symmetric(g-4,g-4,g0)
    c: Coincident(g1,g0)
    c: PointOnObject(g1,g-5)
    c: Coincident(g2,g1)
    c: Coincident(g2,g-5)
    c: Coincident(g3,g2)
    c: Coincident(g3,g-4)
    c: Coincident(g4,g3)
    c: Coincident(g4,g0)
    c: DistanceY(g1,g-5) = 0.7
    c: DistanceY(g0,g-3) = 0.7
    c: Radius(g1) = 4
    c: Radius(g0) = 4
FEATURE [PartDesign::Pocket] Pocket126
  BaseFeature = -> Pad229
  Direction = (1,0,0)
  Length = 5
  Length2 = 5
  Profile = -> Sketch344
  ReferenceAxis = -> Sketch344 [N_Axis]
  Refine = true
  Suppressed = false
  Type = 0
FEATURE [PartDesign::SubShapeBinder] Binder007
  BindCopyOnChange = 0
  BindMode = 2
  ClaimChildren = false
  Context = -> Part [Body019.Binder007.]
  Fuse = false
  MakeFace = true
  OffsetFill = false
  OffsetIntersection = false
  OffsetJoinType = 0
  OffsetOpenResult = false
  PartialLoad = false
  Refine = true
  Relative = true
  _Version = 2
FEATURE [Sketcher::SketchObject] Sketch349
  ArcFitTolerance = 1e-06
  AttachmentSupport = -> [Binder007]
  ExternalGeometry = -> [Binder007]
  FullyConstrained = true
  MakeInternals = false
  MapMode = 5
  Placement = pos=(0,0,-2.5) rot=(1,0,0;3.14159rad)
  sketch-geometry (6):
    g0: LineSegment StartX=-4.75 StartY=2.2 StartZ=0 EndX=-3.5 EndY=2.2 EndZ=0
    g1: LineSegment StartX=-4.75 StartY=2.2 StartZ=0 EndX=-5.75 EndY=0.901388 EndZ=0
    g2: LineSegment StartX=-4.75 StartY=-2.2 StartZ=0 EndX=-3.5 EndY=-2.2 EndZ=0
    g3: LineSegment StartX=-4.75 StartY=-2.2 StartZ=0 EndX=-5.75 EndY=-0.901388 EndZ=0
    g4: ArcOfCircle CenterX=-4.24999 CenterY=-1e-16 CenterZ=0 NormalX=0 NormalY=0 NormalZ=1 AngleXU=0 Radius=1.75001 StartAngle=2.6005 EndAngle=3.68269
    g5: LineSegment StartX=-3.5 StartY=2.2 StartZ=0 EndX=-3.5 EndY=-2.2 EndZ=0
  constraints (15):
    c: Coincident(g0,g-5)
    c: PointOnObject(g0,g-3)
    c: Horizontal(g0)
    c: Coincident(g1,g0)
    c: Coincident(g1,g-6)
    c: Coincident(g2,g-7)
    c: PointOnObject(g2,g-3)
    c: Horizontal(g2)
    c: Coincident(g3,g2)
    c: Coincident(g3,g-7)
    c: Coincident(g4,g1)
    c: Coincident(g4,g3)
    c: Tangent(g4,g-6)
    c: Coincident(g5,g0)
    c: Coincident(g5,g2)
FEATURE [PartDesign::Pad] Pad232
  Direction = (0,0,-1)
  Length = 1.7
  Length2 = 10
  Profile = -> Sketch349
  ReferenceAxis = -> Sketch349 [N_Axis]
  Refine = true
  Suppressed = false
  Type = 0
FEATURE [Sketcher::SketchObject] Sketch350
  ArcFitTolerance = 1e-06
  AttachmentSupport = -> [Pad232]
  ExternalGeometry = -> [Pad232]
  FullyConstrained = true
  MakeInternals = false
  MapMode = 5
  Placement = pos=(-3.5,3e-16,0) rot=(0.57735,0.57735,0.57735;2.0944rad)
  sketch-geometry (5):
    g0: LineSegment StartX=2.2 StartY=-4.2 StartZ=0 EndX=-2.2 EndY=-4.2 EndZ=0
    g1: LineSegment StartX=-2.2 StartY=-4.2 StartZ=0 EndX=-2.2 EndY=-2.9 EndZ=0
    g2: LineSegment StartX=2.2 StartY=-4.2 StartZ=0 EndX=2.2 EndY=-2.9 EndZ=0
    g3: ArcOfCircle CenterX=-0.828312 CenterY=-0.286702 CenterZ=0 NormalX=0 NormalY=0 NormalZ=1 AngleXU=0 Radius=4 StartAngle=4.92098 EndAngle=5.57122
    g4: ArcOfCircle CenterX=0.828312 CenterY=-0.286702 CenterZ=0 NormalX=0 NormalY=0 NormalZ=1 AngleXU=0 Radius=4 StartAngle=3.85356 EndAngle=4.5038
  constraints (14):
    c: Coincident(g0,g-4)
    c: Coincident(g0,g-5)
    c: Coincident(g1,g0)
    c: PointOnObject(g1,g-5)
    c: Coincident(g2,g0)
    c: PointOnObject(g2,g-4)
    c: Coincident(g3,g2)
    c: Symmetric(g0,g0,g3)
    c: Coincident(g4,g3)
    c: Coincident(g4,g1)
    c: DistanceY(g2,g-4) = 0.4
    c: DistanceY(g1,g-5) = 0.4
    c: Radius(g3) = 4
    c: Radius(g4) = 4
FEATURE [PartDesign::Pocket] Pocket129
  BaseFeature = -> Pad232
  Direction = (-1,0,0)
  Length = 5
  Length2 = 5
  Profile = -> Sketch350
  ReferenceAxis = -> Sketch350 [N_Axis]
  Refine = true
  Suppressed = false
  Type = 0
FEATURE [PartDesign::Body] Body019  label="Eyes"
  AllowCompound = false
  Group = -> [Binder007,Sketch349,Pad232,Sketch350,Pocket129]
  Origin = -> Origin020
  Tip = -> Pocket129
FEATURE [PartDesign::SubShapeBinder] Binder008
  BindCopyOnChange = 0
  BindMode = 2
  ClaimChildren = false
  Context = -> Part [Body020.Binder008.]
  Fuse = false
  MakeFace = true
  OffsetFill = false
  OffsetIntersection = false
  OffsetJoinType = 0
  OffsetOpenResult = false
  PartialLoad = false
  Refine = true
  Relative = true
  _Version = 2
FEATURE [Sketcher::SketchObject] Sketch357
  ArcFitTolerance = 1e-06
  AttachmentSupport = -> [Binder008]
  ExternalGeometry = -> [Binder008]
  FullyConstrained = true
  MakeInternals = false
  MapMode = 5
  Placement = pos=(-6e-16,-1,0) rot=(1,0,0;1.5708rad)
  sketch-geometry (9):
    g0: LineSegment StartX=-0.75 StartY=-1.5 StartZ=0 EndX=-0.285898 EndY=-1.5 EndZ=0
    g1: LineSegment StartX=-0.285898 StartY=-1.5 StartZ=0 EndX=-0.285898 EndY=-3.5 EndZ=0
    g2: LineSegment StartX=-0.285898 StartY=-3.5 StartZ=0 EndX=-0.717949 EndY=-3.5 EndZ=0
    g3: LineSegment StartX=-0.717949 StartY=-3.5 StartZ=0 EndX=-0.717949 EndY=-3.7 EndZ=0
    g4: LineSegment StartX=-0.717949 StartY=-3.7 StartZ=0 EndX=-1.51795 EndY=-3.7 EndZ=0
    g5: LineSegment StartX=-1.51795 StartY=-3.7 StartZ=0 EndX=-1.51795 EndY=-3.5 EndZ=0
    g6: LineSegment StartX=-1.51795 StartY=-3.5 StartZ=0 EndX=-1.25 EndY=-2.5 EndZ=0
    g7: LineSegment StartX=-1.25 StartY=-2.5 StartZ=0 EndX=-0.75 EndY=-2.5 EndZ=0
    g8: LineSegment StartX=-0.75 StartY=-2.5 StartZ=0 EndX=-0.75 EndY=-1.5 EndZ=0
  constraints (18):
    c: Coincident(g0,g-4)
    c: Coincident(g0,g-12)
    c: Coincident(g1,g0)
    c: Coincident(g1,g-12)
    c: Coincident(g2,g1)
    c: Coincident(g2,g-11)
    c: Coincident(g3,g2)
    c: Coincident(g3,g-10)
    c: Coincident(g4,g3)
    c: Coincident(g4,g-9)
    c: Coincident(g5,g4)
    c: Coincident(g5,g-9)
    c: Coincident(g6,g5)
    c: Coincident(g6,g-6)
    c: Coincident(g7,g6)
    c: Coincident(g7,g-5)
    c: Coincident(g8,g7)
    c: Coincident(g8,g0)
FEATURE [PartDesign::Pad] Pad238
  Direction = (0,-1,2e-16)
  Length = 2
  Length2 = 10
  Profile = -> Sketch357
  ReferenceAxis = -> Sketch357 [N_Axis]
  Refine = true
  Reversed = true
  Suppressed = false
  Type = 0
FEATURE [Sketcher::SketchObject] Sketch358
  ArcFitTolerance = 1e-06
  AttachmentSupport = -> [Pad238]
  ExternalGeometry = -> [Pad238]
  FullyConstrained = true
  MakeInternals = false
  MapMode = 5
  Placement = pos=(0,-8e-16,-3.5) rot=(1,0,0;3.14159rad)
  sketch-geometry (6):
    g0: ArcOfCircle CenterX=-0.717949 CenterY=0.7 CenterZ=0 NormalX=0 NormalY=0 NormalZ=1 AngleXU=0 Radius=0.3 StartAngle=0 EndAngle=1.5708
    g1: ArcOfCircle CenterX=-0.717949 CenterY=-0.7 CenterZ=0 NormalX=0 NormalY=0 NormalZ=1 AngleXU=0 Radius=0.3 StartAngle=4.71239 EndAngle=6.28319
    g2: LineSegment StartX=-0.417949 StartY=0.7 StartZ=0 EndX=-0.417949 EndY=-0.7 EndZ=0
    g3: LineSegment StartX=-0.717949 StartY=1 StartZ=0 EndX=-0.717949 EndY=-1 EndZ=0
    g4: LineSegment [constr] StartX=-0.417949 StartY=0.7 StartZ=0 EndX=-0.717949 EndY=0.7 EndZ=0
    g5: LineSegment [constr] StartX=-0.417949 StartY=-0.7 StartZ=0 EndX=-0.717949 EndY=-0.7 EndZ=0
  constraints (16):
    c: Coincident(g0,g-4)
    c: Coincident(g1,g-5)
    c: Coincident(g2,g0)
    c: Coincident(g2,g1)
    c: Vertical(g2)
    c: Coincident(g3,g0)
    c: Coincident(g3,g1)
    c: PointOnObject(g0,g3)
    c: Radius(g1) = 0.3
    c: Radius(g0) = 0.3
    c: Coincident(g4,g0)
    c: Coincident(g4,g0)
    c: Horizontal(g4)
    c: Coincident(g5,g1)
    c: Coincident(g5,g1)
    c: Horizontal(g5)
FEATURE [PartDesign::Pad] Pad239
  BaseFeature = -> Pad238
  Direction = (0,0,-1)
  Length = 0.2
  Length2 = 10
  Profile = -> Sketch358
  ReferenceAxis = -> Sketch358 [N_Axis]
  Refine = true
  Suppressed = false
  Type = 0
FEATURE [Sketcher::SketchObject] Sketch359
  ArcFitTolerance = 1e-06
  AttachmentSupport = -> [Pad239]
  ExternalGeometry = -> [Pad239]
  FullyConstrained = true
  MakeInternals = false
  MapMode = 5
  Placement = pos=(0,0,-3.7) rot=(1,0,0;3.14159rad)
  sketch-geometry (12):
    g0: ArcOfCircle CenterX=-1.51795 CenterY=1.6e-15 CenterZ=0 NormalX=0 NormalY=0 NormalZ=1 AngleXU=0 Radius=0.3 StartAngle=4.71239 EndAngle=7.85398
    g1: LineSegment StartX=-1.51795 StartY=-0.6 StartZ=0 EndX=-1.11795 EndY=-0.6 EndZ=0
    g2: LineSegment StartX=-1.51795 StartY=0.6 StartZ=0 EndX=-1.11795 EndY=0.6 EndZ=0
    g3: ArcOfCircle CenterX=-1.11795 CenterY=0.3 CenterZ=0 NormalX=0 NormalY=0 NormalZ=1 AngleXU=0 Radius=0.3 StartAngle=1e-16 EndAngle=1.5708
    g4: ArcOfCircle CenterX=-1.11795 CenterY=-0.3 CenterZ=0 NormalX=0 NormalY=0 NormalZ=1 AngleXU=0 Radius=0.3 StartAngle=4.71239 EndAngle=6.28319
    g5: LineSegment StartX=-0.817949 StartY=0.3 StartZ=0 EndX=-0.817949 EndY=-0.3 EndZ=0
    g6: LineSegment StartX=-1.51795 StartY=0.6 StartZ=0 EndX=-1.51795 EndY=0.3 EndZ=0
    g7: LineSegment StartX=-1.51795 StartY=-0.3 StartZ=0 EndX=-1.51795 EndY=-0.6 EndZ=0
    g8: LineSegment [constr] StartX=-1.11795 StartY=0.6 StartZ=0 EndX=-1.11795 EndY=0.3 EndZ=0
    g9: LineSegment [constr] StartX=-1.11795 StartY=0.3 StartZ=0 EndX=-0.817949 EndY=0.3 EndZ=0
    g10: LineSegment [constr] StartX=-0.817949 StartY=-0.3 StartZ=0 EndX=-1.11795 EndY=-0.3 EndZ=0
    g11: LineSegment [constr] StartX=-1.11795 StartY=-0.3 StartZ=0 EndX=-1.11795 EndY=-0.6 EndZ=0
  constraints (36):
    c: PointOnObject(g0,g-3)
    c: PointOnObject(g0,g-3)
    c: Radius(g0) = 0.3
    c: PointOnObject(g0,g-3)
    c: DistanceY(g-3,g-3) = 2
    c: DistanceY(g-3,g0) = 1
    c: PointOnObject(g1,g-3)
    c: Horizontal(g1)
    c: PointOnObject(g2,g-3)
    c: Horizontal(g2)
    c: Coincident(g3,g2)
    c: Coincident(g4,g1)
    c: Coincident(g5,g3)
    c: Coincident(g5,g4)
    c: Vertical(g5)
    c: Coincident(g6,g2)
    c: Coincident(g6,g0)
    c: Coincident(g7,g0)
    c: Coincident(g7,g1)
    c: DistanceX(g1,g1) = 0.4
    c: DistanceX(g2,g2) = 0.4
    c: DistanceY(g6,g6) = 0.3
    c: DistanceY(g7,g7) = 0.3
    c: Coincident(g8,g2)
    c: Coincident(g8,g3)
    c: Coincident(g9,g3)
    c: Coincident(g9,g3)
    c: Coincident(g10,g4)
    c: Coincident(g10,g4)
    c: Coincident(g11,g4)
    c: Coincident(g11,g1)
    c: Vertical(g11)
    c: Horizontal(g9)
    c: Horizontal(g10)
    c: Vertical(g8)
    c: Radius(g4) = 0.3
FEATURE [PartDesign::Pocket] Pocket137
  BaseFeature = -> Pad239
  Direction = (0,0,1)
  Length = 0.2
  Length2 = 5
  Profile = -> Sketch359
  ReferenceAxis = -> Sketch359 [N_Axis]
  Refine = true
  Suppressed = false
  Type = 0
FEATURE [Sketcher::SketchObject] Sketch361
  ArcFitTolerance = 1e-06
  AttachmentSupport = -> [Pocket126]
  ExternalGeometry = -> [Pocket126]
  FullyConstrained = true
  MakeInternals = false
  MapMode = 5
  Placement = pos=(0,0,-2.5) rot=(0,0,1;0rad)
  sketch-geometry (4):
    g0: LineSegment StartX=-8 StartY=2.2 StartZ=0 EndX=-8 EndY=-2.2 EndZ=0
    g1: LineSegment StartX=-8 StartY=-2.2 StartZ=0 EndX=-7.95 EndY=-2.2 EndZ=0
    g2: LineSegment StartX=-7.95 StartY=-2.2 StartZ=0 EndX=-7.95 EndY=2.2 EndZ=0
    g3: LineSegment StartX=-7.95 StartY=2.2 StartZ=0 EndX=-8 EndY=2.2 EndZ=0
  constraints (11):
    c: Coincident(g0,g1)
    c: Coincident(g1,g2)
    c: Coincident(g2,g3)
    c: Coincident(g3,g0)
    c: Vertical(g0)
    c: Vertical(g2)
    c: Horizontal(g1)
    c: Horizontal(g3)
    c: Coincident(g0,g-8)
    c: PointOnObject(g1,g-7)
    c: DistanceX(g1,g1) = 0.05
FEATURE [PartDesign::Pocket] Pocket139
  BaseFeature = -> Pocket126
  Direction = (0,0,-1)
  Length = 5
  Length2 = 5
  Profile = -> Sketch361
  ReferenceAxis = -> Sketch361 [N_Axis]
  Refine = true
  Suppressed = false
  Type = 0
FEATURE [PartDesign::Body] Body016  label="Mouth"
  AllowCompound = false
  Group = -> [Binder004,Sketch343,Pad229,Sketch344,Pocket126,Sketch361,Pocket139]
  Origin = -> Origin017
  Tip = -> Pocket139
FEATURE [PartDesign::Body] Body009  label="Main_Head"
  AllowCompound = false
  Group = -> [Sketch256,Pad154,Sketch257,Pocket106,Sketch258,Pad155,Sketch259,Pocket107,Sketch260,Pocket108,Sketch261,Pad156,Sketch262,Pad157,Fillet009,Sketch263,Pocket109,Sketch265,Pad158,Sketch266,Pad159,Sketch267,Pad160,Sketch268,Pad161,Sketch269,Pad162,Sketch270,Pocket111,Sketch271,Pocket112,Sketch272,Pad163,Sketch273,Pad164,Sketch274,Pad165,Draft,Sketch275,Pocket113,Sketch276,Pad166,Pad167,Sketch277,+9 more]
  Origin = -> Origin009
  Placement = pos=(-8,4,-5) rot=(0,0,1;3.14159rad)
  Tip = -> Pocket140
FEATURE [Sketcher::SketchObject] Sketch365
  ArcFitTolerance = 1e-06
  AttachmentSupport = -> [Pocket137]
  ExternalGeometry = -> [Pocket137]
  FullyConstrained = true
  MakeInternals = false
  MapMode = 5
  Placement = pos=(0,1,-2e-16) rot=(0,0.707107,0.707107;3.14159rad)
  sketch-geometry (4):
    g0: LineSegment StartX=0.75 StartY=-1.5 StartZ=0 EndX=0.75 EndY=-2.5 EndZ=0
    g1: LineSegment StartX=0.75 StartY=-2.5 StartZ=0 EndX=1.25 EndY=-2.5 EndZ=0
    g2: LineSegment StartX=1.25 StartY=-2.5 StartZ=0 EndX=1.25 EndY=-1.5 EndZ=0
    g3: LineSegment StartX=1.25 StartY=-1.5 StartZ=0 EndX=0.75 EndY=-1.5 EndZ=0
  constraints (10):
    c: Coincident(g0,g1)
    c: Coincident(g1,g2)
    c: Coincident(g2,g3)
    c: Coincident(g3,g0)
    c: Vertical(g0)
    c: Vertical(g2)
    c: Horizontal(g1)
    c: Horizontal(g3)
    c: Coincident(g0,g-3)
    c: Coincident(g1,g-4)
FEATURE [PartDesign::Pad] Pad244
  BaseFeature = -> Pocket137
  Direction = (0,1,-2e-16)
  Length = 2
  Length2 = 10
  Profile = -> Sketch365
  ReferenceAxis = -> Sketch365 [N_Axis]
  Refine = true
  Reversed = true
  Suppressed = false
  Type = 0
FEATURE [PartDesign::Body] Body020  label="Forehead"
  AllowCompound = false
  Group = -> [Binder008,Sketch357,Pad238,Sketch358,Pad239,Sketch359,Pocket137,Sketch365,Pad244]
  Origin = -> Origin021
  Tip = -> Pad244
PROVENANCE & LICENSES
A FreeCAD (.FCStd) document from a public repository crawl; recipes are the document's own serialized feature recipes (and, for linked parts, companion documents' recipes).
License: as declared in the source repository (recorded in the dataset sidecar).
